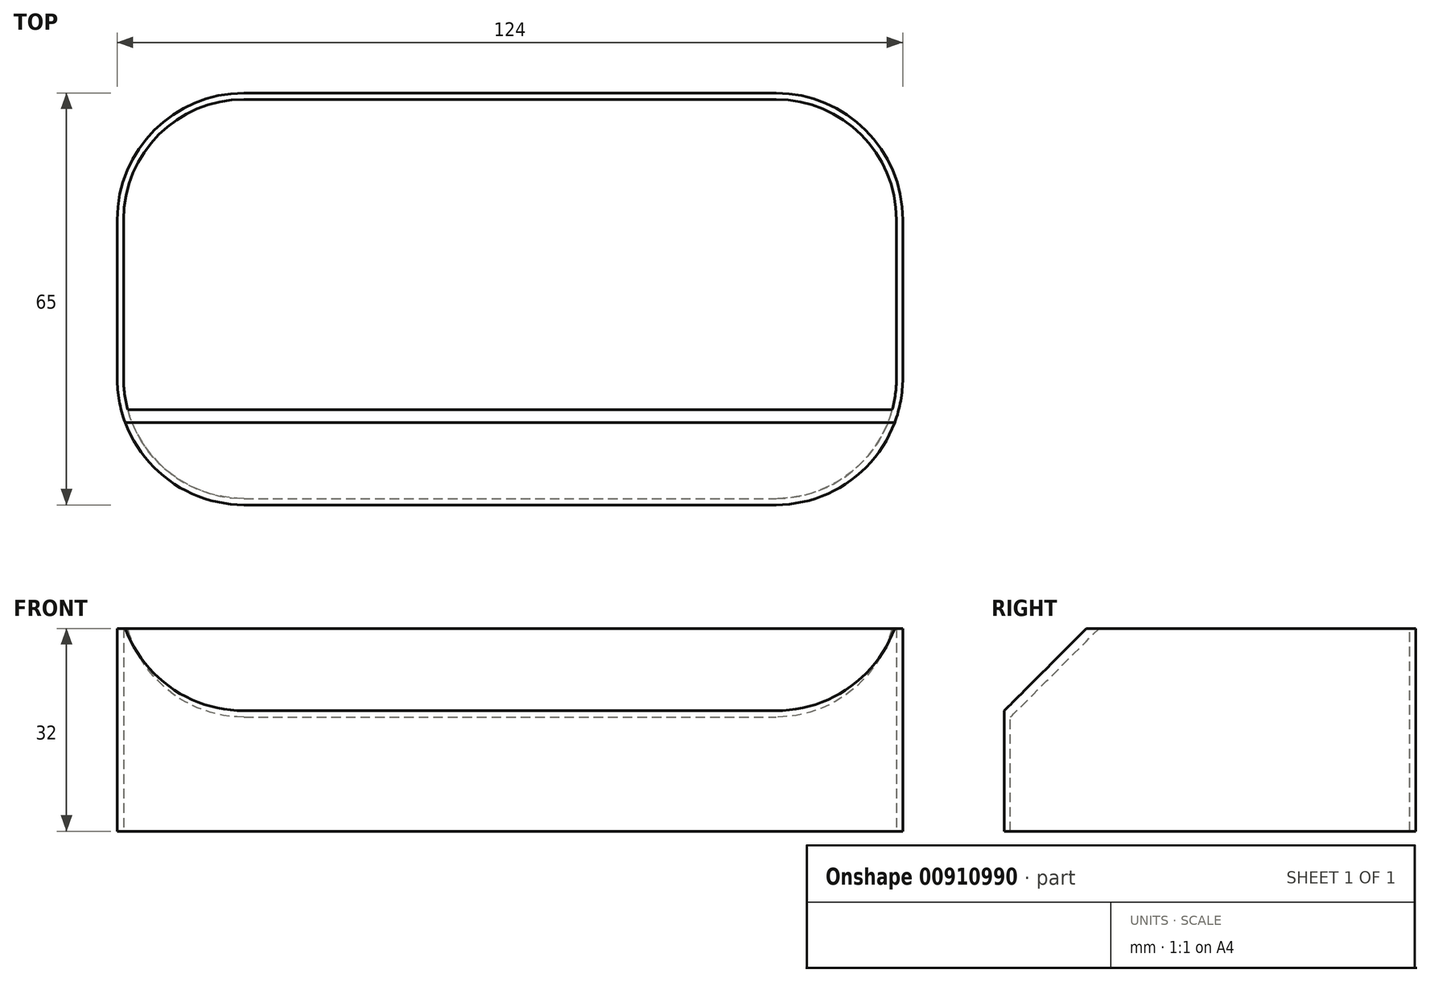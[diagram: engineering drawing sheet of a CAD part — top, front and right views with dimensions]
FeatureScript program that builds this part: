
annotation { "Feature Type Name" : "Feature", "Feature Type Description" : "" }
export const myFeature = defineFeature(function(context is Context, id is Id, definition is map)
    precondition{}
    {
        {
            var Q0;
            Q0=qCreatedBy(makeId("Top.planeOp"),FACE);
            var sketch = newSketch(context, id + "F0", { "sketchPlane" : qUnion([Q0])});
            skLineSegment(sketch, "E0.bottom", {"start": v(0, 0) * mm, "end": v(124, 0) * mm});
            skLineSegment(sketch, "E0.top", {"start": v(0, -65) * mm, "end": v(124, -65) * mm});
            skLineSegment(sketch, "E0.left", {"start": v(0, 0) * mm, "end": v(0, -65) * mm});
            skLineSegment(sketch, "E0.right", {"start": v(124, 0) * mm, "end": v(124, -65) * mm});
            skSolve(sketch);
        }
        {
            var Q0;
            Q0 = qSketchRegion(id + "F0", true);
            extrude(context, id + "F1", {"entities" : qUnion([Q0]), "depth" : 32 * mm, "offsetDistance" : 25 * mm});
        }
        {
            var Q0;
            Q0=makeQuery(id+"F1.opExtrude","SWEPT_EDGE",EDGE,{"disambiguationData":[OSD([sQuery(id+"F0.wireOp",EDGE,"E0.top"),sQuery(id+"F0.wireOp",EDGE,"E0.right")])]});
            var Q1;
            Q1=makeQuery(id+"F1.opExtrude","SWEPT_EDGE",EDGE,{"disambiguationData":[OSD([sQuery(id+"F0.wireOp",EDGE,"E0.bottom"),sQuery(id+"F0.wireOp",EDGE,"E0.right")])]});
            var Q2;
            Q2=makeQuery(id+"F1.opExtrude","SWEPT_EDGE",EDGE,{"disambiguationData":[OSD([sQuery(id+"F0.wireOp",EDGE,"E0.top"),sQuery(id+"F0.wireOp",EDGE,"E0.left")])]});
            var Q3;
            Q3=makeQuery(id+"F1.opExtrude","SWEPT_EDGE",EDGE,{"disambiguationData":[OSD([sQuery(id+"F0.wireOp",EDGE,"E0.bottom"),sQuery(id+"F0.wireOp",EDGE,"E0.left")])]});
            fillet(context, id + "F2", {"entities" : qUnion([Q0, Q1, Q2, Q3]), "radius" : 20 * mm, "tangentPropagation" : true, "allowEdgeOverflow" : false});
        }
        {
            var Q0;
            Q0=makeQuery(id+"F1.opExtrude","CAP_FACE",FACE,{"disambiguationData":[OSD([sQuery(id+"F0.wireOp",EDGE,"E0.bottom"),sQuery(id+"F0.wireOp",EDGE,"E0.top"),sQuery(id+"F0.wireOp",EDGE,"E0.left"),sQuery(id+"F0.wireOp",EDGE,"E0.right")])],"isStart":false});
            shell(context, id + "F3", {"entities" : qUnion([Q0]), "thickness" : 1 * mm});
        }
        {
            var Q0;
            Q0=makeQuery(id+"F3.opShell","OFFSET_FACE",FACE,{"disambiguationData":[OSD([sQuery(id+"F0.wireOp",EDGE,"E0.bottom"),sQuery(id+"F0.wireOp",EDGE,"E0.top"),sQuery(id+"F0.wireOp",EDGE,"E0.left"),sQuery(id+"F0.wireOp",EDGE,"E0.right")])]});
            extrude(context, id + "F4", {"entities" : qUnion([Q0]), "operationType" : NewBodyOperationType.REMOVE, "endBound" : BoundingType.THROUGH_ALL, "oppositeDirection" : true, "depth" : 25 * mm, "offsetDistance" : 25 * mm});
        }
        {
            var Q0;
            Q0=makeQuery(id+"F1.opExtrude","SWEPT_FACE",FACE,{"disambiguationData":[OSD([sQuery(id+"F0.wireOp",EDGE,"E0.top")])]});
            var sketch = newSketch(context, id + "F5", { "sketchPlane" : qUnion([Q0])});
            skLineSegment(sketch, "E1.bottom", {"start": v(1, 17) * mm, "end": v(123, 17) * mm});
            skLineSegment(sketch, "E1.top", {"start": v(1, 32) * mm, "end": v(123, 32) * mm});
            skLineSegment(sketch, "E1.left", {"start": v(1, 17) * mm, "end": v(1, 32) * mm});
            skLineSegment(sketch, "E1.right", {"start": v(123, 17) * mm, "end": v(123, 32) * mm});
            skSolve(sketch);
        }
        {
            var Q0;
            Q0 = qSketchRegion(id + "F5", true);
            extrude(context, id + "F6", {"entities" : qUnion([Q0]), "operationType" : NewBodyOperationType.ADD, "oppositeDirection" : true, "depth" : 15 * mm, "offsetDistance" : 25 * mm});
        }
        {
            var Q0;
            Q0=makeQuery(id+"F6.opExtrude","CAP_EDGE",EDGE,{"disambiguationData":[OSD([sQuery(id+"F5.wireOp",EDGE,"E1.left")])],"isStart":true});
            var Q1;
            Q1=makeQuery(id+"F6.opExtrude","CAP_EDGE",EDGE,{"disambiguationData":[OSD([sQuery(id+"F5.wireOp",EDGE,"E1.right")])],"isStart":true});
            fillet(context, id + "F7", {"entities" : qUnion([Q0, Q1]), "radius" : 20 * mm, "tangentPropagation" : true, "allowEdgeOverflow" : false});
        }
        {
            var Q0;
            Q0=makeQuery(id+"F6.boolean.opBoolean","MERGE",FACE,{"derivedFrom":[makeQuery(id+"F1.opExtrude","CAP_FACE",FACE,{"disambiguationData":[OSD([sQuery(id+"F0.wireOp",EDGE,"E0.bottom"),sQuery(id+"F0.wireOp",EDGE,"E0.top"),sQuery(id+"F0.wireOp",EDGE,"E0.left"),sQuery(id+"F0.wireOp",EDGE,"E0.right")])],"isStart":false}),makeQuery(id+"F6.opExtrude","SWEPT_FACE",FACE,{"disambiguationData":[OSD([sQuery(id+"F5.wireOp",EDGE,"E1.top")])]})]});
            var sketch = newSketch(context, id + "F8", { "sketchPlane" : qUnion([Q0])});
            skLineSegment(sketch, "E2.bottom", {"start": v(0, -51) * mm, "end": v(150, -51) * mm});
            skLineSegment(sketch, "E2.top", {"start": v(0, -71) * mm, "end": v(150, -71) * mm});
            skLineSegment(sketch, "E2.left", {"start": v(0, -51) * mm, "end": v(0, -71) * mm});
            skLineSegment(sketch, "E2.right", {"start": v(150, -51) * mm, "end": v(150, -71) * mm});
            skSolve(sketch);
        }
        {
            var Q0;
            Q0 = qSketchRegion(id + "F8", true);
            extrude(context, id + "F9", {"entities" : qUnion([Q0]), "operationType" : NewBodyOperationType.REMOVE, "oppositeDirection" : true, "depth" : 14 * mm, "offsetDistance" : 25 * mm});
        }
        {
            var Q0;
            Q0=makeQuery(id+"F9.boolean.opBoolean","COPY",EDGE,{"derivedFrom":makeQuery(id+"F9.opExtrude","CAP_EDGE",EDGE,{"disambiguationData":[OSD([sQuery(id+"F8.wireOp",EDGE,"E2.bottom")])],"isStart":false})});
            chamfer(context, id + "F10", {"entities" : qUnion([Q0]), "width" : 15 * mm, "tangentPropagation" : true});
        }
        {
            var Q0;
            Q0=makeQuery(id+"F6.opExtrude","CAP_EDGE",EDGE,{"disambiguationData":[OSD([sQuery(id+"F5.wireOp",EDGE,"E1.bottom")])],"isStart":false});
            chamfer(context, id + "F11", {"entities" : qUnion([Q0]), "width" : 15 * mm, "tangentPropagation" : true});
        }
    });
